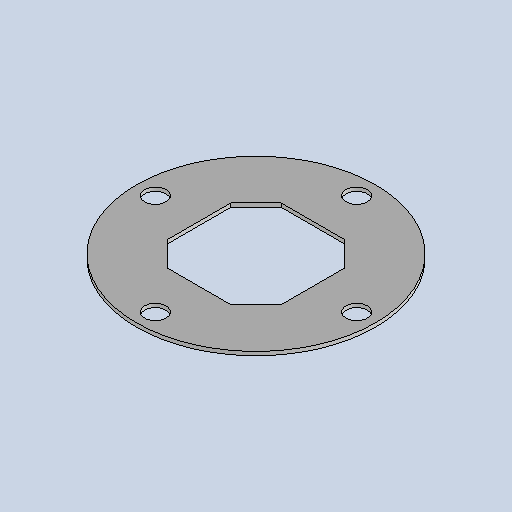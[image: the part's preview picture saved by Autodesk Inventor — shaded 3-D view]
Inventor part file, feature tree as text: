
AUTODESK INVENTOR PART (.ipt)
format: ipt  version: 2025.1 (Build 291241020, 241B)  size: 167,424 bytes
history: native  units: mm
features: other x4, sketch x2, sheet_metal_op x1, pattern_circular x1
ambient origin geometry x8: Origin, YZ Plane, XZ Plane, XY Plane, X Axis, Y Axis, Z Axis, Center Point
bodies: Body1 (feature_tree)
feature tree (8):
  sheet_metal_op  "Face3"
  pattern_circular  "Circular Pattern1"  Count=50  [1 undecoded]
  other  "Corner Chamfer2"
  sketch  "Sketch1"  dims[d156=3.0mm]
  other  "Plate5"
  sketch  "Sketch7"  dims[d157=190.0mm d158=90.0mm d159=90.0mm d160=17.0mm d161=80.0mm d162=3.0mm d163=0.0mm d164=40.0mm d165=360.0deg d167=20.0mm d168=6.0mm d169=45.0deg]
  other  "Cut1"
  other  "Definition1"
note: 1 required parameter value undecoded (feature->parameter linkage not recoverable at this tier; creation-order binding heuristic only, values carry confidence <= 0.55)
